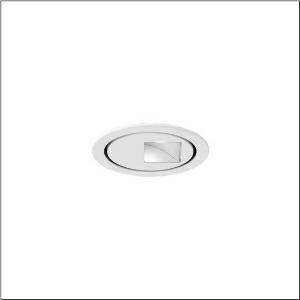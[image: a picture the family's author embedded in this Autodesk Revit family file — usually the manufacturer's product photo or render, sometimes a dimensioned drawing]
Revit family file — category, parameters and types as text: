
# Revit family: lunis_11_micro_round_51dj11cd1wm21
name_source: partatom
category: Lighting Fixtures
units: mm (PartAtom-declared; Revit-internal decimal feet)

## family parameters
Cut with Voids When Loaded = No
Host = Face
Light Source = No
Part Type = Normal
Room Calculation Point = No
Round Connector Dimension = Use Diameter
Shared = No

## types (1)
- Lunis 11 micro round (1 x LED 3000K / CRI = 90 (unbekannt), 1100 lm, 3000K)
    Apparent Load = 20 VA
    CIE Flux Codes = 42 75 96 100 100
    Color Rendering = 90
    Color Temperature = 3000K
    Default Elevation = 1800 mm
    Description = Lunis 11 micro round, downlight, light control with wallwasher, of highly reflective aluminium, highly specular, light emission: direct distribution, LED rated luminous flux: 1.100lm, light colour: 930, with terminal, 5-pole, mains connection: 220..230V, AC, 50/60Hz, LED module, of aluminium, highly specular, white, diameter: 114mm, clamping range: 1..40mm, recessing ring, of plastic, traffic white (RAL 9016), protection rating (complete): IP20, insulation class (complete): insulation class II (safety insulation), certification: CE, permissible ambient temperature for indoor applications: 0..+35°C, packaging unit: 1 piece
    Height = 0 mm  [stored 0 ft]
    Lamp = 1 x LED 3000K / CRI >= 90 (unbekannt)
    Lamp Light Flux = 1100 lm
    Lamp count = 1
    Length = 114 mm
    Luminous efficacy = 56 lm/W
    Manufacturer = Siteco
    ModVariant = No
    Model = 51DJ11CD1WM21
    Mounting Place = Ceiling
    Mounting Type = Recessed
    Number of Poles = 1
    OnlyDefault = Yes
    Power Factor = 1
    Product Name = Lunis 11 micro round
    Product group = downlight
    ProductGroupID = 401
    Protection Class = Protection class II
    Protection Degree = IP 20
    RLX_Detail_Level = 1
    RLX_Emergency_Light_Flux = 0 lm
    RLX_Emergency_Type = 0
    RLX_Emergency_Type_DB = No
    RlxData = <blob elided: 40265 chars, md5=41ae872b>
    Socket = socket
    Standby Power = 0 W
    System Light Flux = 1100 lm
    System Power = 20 W
    Type Comments = Product without accessories
    Type Image = l_1004773.jpg
    URL = http://relux.com
    VarID = ---
    Voltage = 0 V
    Weight = 0.00 kg
    Width = 114 mm

note: [stored X ft] marks values corroborated as IEEE doubles in the binary element streams (Revit-internal decimal feet)

## geometry (parser evidence)
native form markers: Blend x4, Sweep x10
no freeform markers — native parametric forms only
